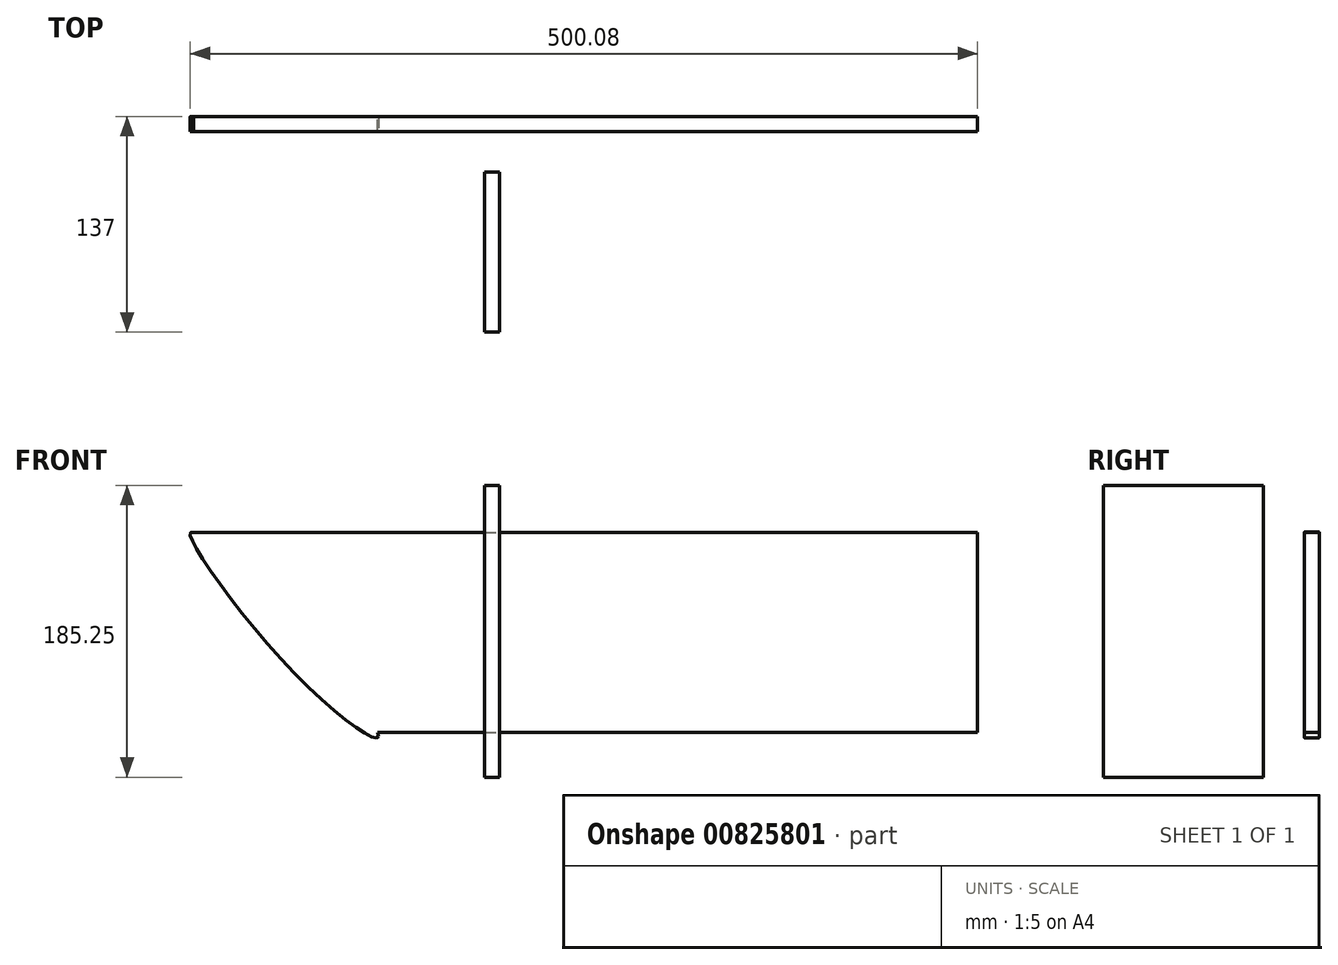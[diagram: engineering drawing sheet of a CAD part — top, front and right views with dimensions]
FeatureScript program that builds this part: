
annotation { "Feature Type Name" : "Feature", "Feature Type Description" : "" }
export const myFeature = defineFeature(function(context is Context, id is Id, definition is map)
    precondition{}
    {
        {
            var Q0;
            Q0=qCreatedBy(makeId("Front.planeOp"),FACE);
            var sketch = newSketch(context, id + "F0", { "sketchPlane" : qUnion([Q0])});
            skLineSegment(sketch, "E0.bottom", {"start": v(-67.76, 69.7) * mm, "end": v(313.24, 69.7) * mm});
            skLineSegment(sketch, "E0.top", {"start": v(-67.76, -57.3) * mm, "end": v(313.24, -57.3) * mm});
            skLineSegment(sketch, "E0.left", {"start": v(-67.76, 69.7) * mm, "end": v(-67.76, -57.3) * mm});
            skLineSegment(sketch, "E0.right", {"start": v(313.24, 69.7) * mm, "end": v(313.24, -57.3) * mm});
            skLineSegment(sketch, "E1", {"start": v(-67.76, 69.7) * mm, "end": v(-184.65, 69.7) * mm});
            skFitSpline(sketch, "E2", {"points": [v(-184.65, 69.7) * mm, v(-67.76, -57.3) * mm, v(-118.93, -21.4) * mm, v(-184.65, 69.7) * mm]});
            skLineSegment(sketch, "E3.bottom", {"start": v(300.22, -43.16) * mm, "end": v(-67.76, -43.16) * mm});
            skLineSegment(sketch, "E3.top", {"start": v(300.22, 69.7) * mm, "end": v(-67.76, 69.7) * mm});
            skLineSegment(sketch, "E3.left", {"start": v(300.22, -43.16) * mm, "end": v(300.22, 69.7) * mm});
            skLineSegment(sketch, "E3.right", {"start": v(-67.76, -43.16) * mm, "end": v(-67.76, 69.7) * mm});
            skSolve(sketch);
        }
        {
            var Q0;
            Q0 = qSketchRegion(id + "F0", true);
            extrude(context, id + "F1", {"entities" : qUnion([Q0]), "depth" : 9.52 * mm, "offsetDistance" : 25.4 * mm});
        }
        {
            var Q0;
            Q0=qCreatedBy(makeId("Right.planeOp"),FACE);
            var sketch = newSketch(context, id + "F2", { "sketchPlane" : qUnion([Q0])});
            skLineSegment(sketch, "E4.bottom", {"start": v(-35.4, 99.54) * mm, "end": v(-137, 99.54) * mm});
            skLineSegment(sketch, "E4.top", {"start": v(-35.4, -85.71) * mm, "end": v(-137, -85.71) * mm});
            skLineSegment(sketch, "E4.left", {"start": v(-35.4, 99.54) * mm, "end": v(-35.4, -85.71) * mm});
            skLineSegment(sketch, "E4.right", {"start": v(-137, 99.54) * mm, "end": v(-137, -85.71) * mm});
            skSolve(sketch);
        }
        {
            var Q0;
            Q0 = qSketchRegion(id + "F2", true);
            extrude(context, id + "F3", {"entities" : qUnion([Q0]), "depth" : 9.65 * mm, "offsetDistance" : 25.4 * mm});
        }
    });
